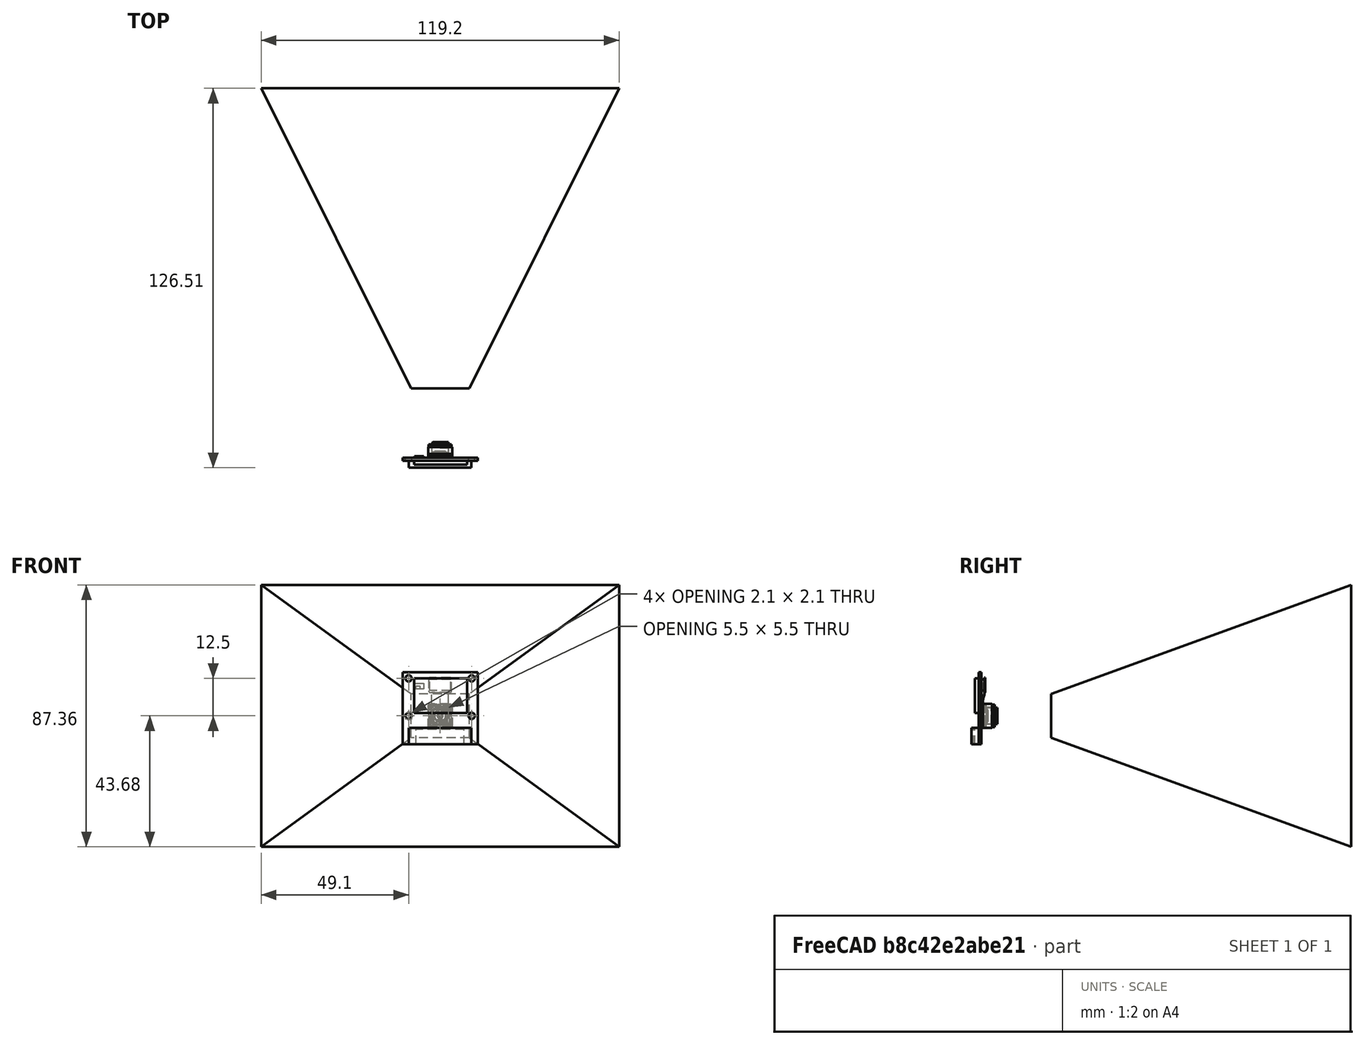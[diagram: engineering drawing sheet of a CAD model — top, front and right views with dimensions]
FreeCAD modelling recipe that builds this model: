
FCSTD DOCUMENT  (FreeCAD 0.16R4945 (Git))
Label: Pi-Camera
License: CreativeCommons Attribution-ShareAlike
LicenseURL: http://creativecommons.org/licenses/by-sa/4.0/
objects: Part::Feature×6, Sketcher::SketchObject×1, PartDesign::Pocket×1, Part::Compound×1, Part::FeaturePython×1
note: 11 computed .brp shape members not serialized (recipe doc carries the construction recipe); baked Part::Feature solids carry a one-line shape summary decoded from their .brp

FEATURE [Part::Feature] Part__Feature  label="OVA5647_FOV"
  Placement = pos=(0.32,0,-0.175) rot=(0,0,1;0rad)
  shape: bbox 8 x 0.6907 x 8 mm, 373 faces (baked)
FEATURE [Part::Feature] Part__Feature001  label="OVA5647_FOV001"
  shape: bbox 8 x 3.95 x 8 mm, 38 faces (baked)
FEATURE [Part::Feature] Part__Feature002  label="OVA5647_FOV002"
  Placement = pos=(0,0.95,0) rot=(0,0,1;3.14159rad)
  shape: bbox 6.3 x 0.35 x 6.3 mm, 6 faces (baked)
FEATURE [Part::Feature] Part__Feature003  label="OVA5647_FOV003"
  Placement = pos=(0,3.95,0) rot=(0,0,1;0rad)
  shape: bbox 6 x 3.35 x 6 mm, 27 faces (baked)
FEATURE [Part::Feature] Part__Feature005  label="OVA5647_FOV005"
  shape: bbox 5.6 x 0.686 x 3.752 mm, 6 faces (baked)
FEATURE [Part::Feature] Part__Feature006  label="OVA5647_FOV006"
  shape: bbox 7.6 x 1.3 x 5 mm, 15 faces (baked)
FEATURE [Sketcher::SketchObject] Sketch001
  Placement = pos=(0,-0.551699,-9.5) rot=(0,1,0;3.14159rad)
  sketch-geometry (4):
    g0: LineSegment StartX=-8 StartY=-2.1 StartZ=0 EndX=8 EndY=-2.1 EndZ=0
    g1: LineSegment StartX=8 StartY=-2.1 StartZ=0 EndX=8 EndY=-2.5 EndZ=0
    g2: LineSegment StartX=8 StartY=-2.5 StartZ=0 EndX=-8 EndY=-2.5 EndZ=0
    g3: LineSegment StartX=-8 StartY=-2.5 StartZ=0 EndX=-8 EndY=-2.1 EndZ=0
  constraints (8):
    c: Coincident(g0,g1)
    c: Coincident(g1,g2)
    c: Coincident(g2,g3)
    c: Coincident(g3,g0)
    c: Horizontal(g0)
    c: Horizontal(g2)
    c: Vertical(g1)
    c: Vertical(g3)
FEATURE [PartDesign::Pocket] Pocket001
  Length = 5
  Placement = pos=(0,-0.551699,0) rot=(0,1,0;3.14159rad)
  Sketch = -> Sketch001
  Type = 0
FEATURE [Part::Compound] Compound
  Links = -> [Part__Feature,Part__Feature005,Part__Feature002,Part__Feature006,Part__Feature001,Pocket001,Part__Feature003]
FEATURE [Part::FeaturePython] FOV_01  # a2plus imported part (geometry in sourceFile) (typed FeaturePython)
  Placement = pos=(0,3.95,0) rot=(0,0,1;0rad)
  fixedPosition = true
  sourceFile = <userpath>/CloudStation/Hobbyprojekte/3D Drucker/CoreXY/Assembly/Parts/!Temp Folder/3D Printer Parts/FOV.FCStd
  timeLastImport = 1444684620
  updateColors = true
